# Revit family: 5LDS6030B75T,B17T,B75B,B17B
name_source: partatom
category: Plumbing Fixtures
revit_build: Autodesk Revit LT 2014 (Build: 20130308_1515(x64)
units: mm (PartAtom-declared; Revit-internal decimal feet)

## types (4) — shared parameters
Assembly Code = D2010710
Keynote = 22 40 00.B3
Manufacturer = Best Bath Systems, Inc.
Type Comments = Barrier Free
URL = http://www.best-bath.com
Unit Width = 5' - 0"

## per-type parameters (varying)
| type | Description | Threshold Height | Unit Height |
| 5LDS6030B75B | Diamond Tile, Beveled Threshold | 0' - 0 3/4" | 6' - 9" |
| 5LDS6030B15B | Diamond Tile, Beveled Threshold | 0' - 1 1/2" | 6' - 9 3/4" |
| 5LDS6030B75T | Diamond Tile, Traditional Bull Nose Threshold | 0' - 0 3/4" | 6' - 9" |
| 5LDS6030B15T | Diamond Tile, Traditionals Bull Nose Threshold | 0' - 1 1/2" | 6' - 9 3/4" |

note: column(s) folded — value = type name in every type: Model

## geometry (parser evidence)
native form markers: Blend x20, Sweep x1
no freeform markers — native parametric forms only
